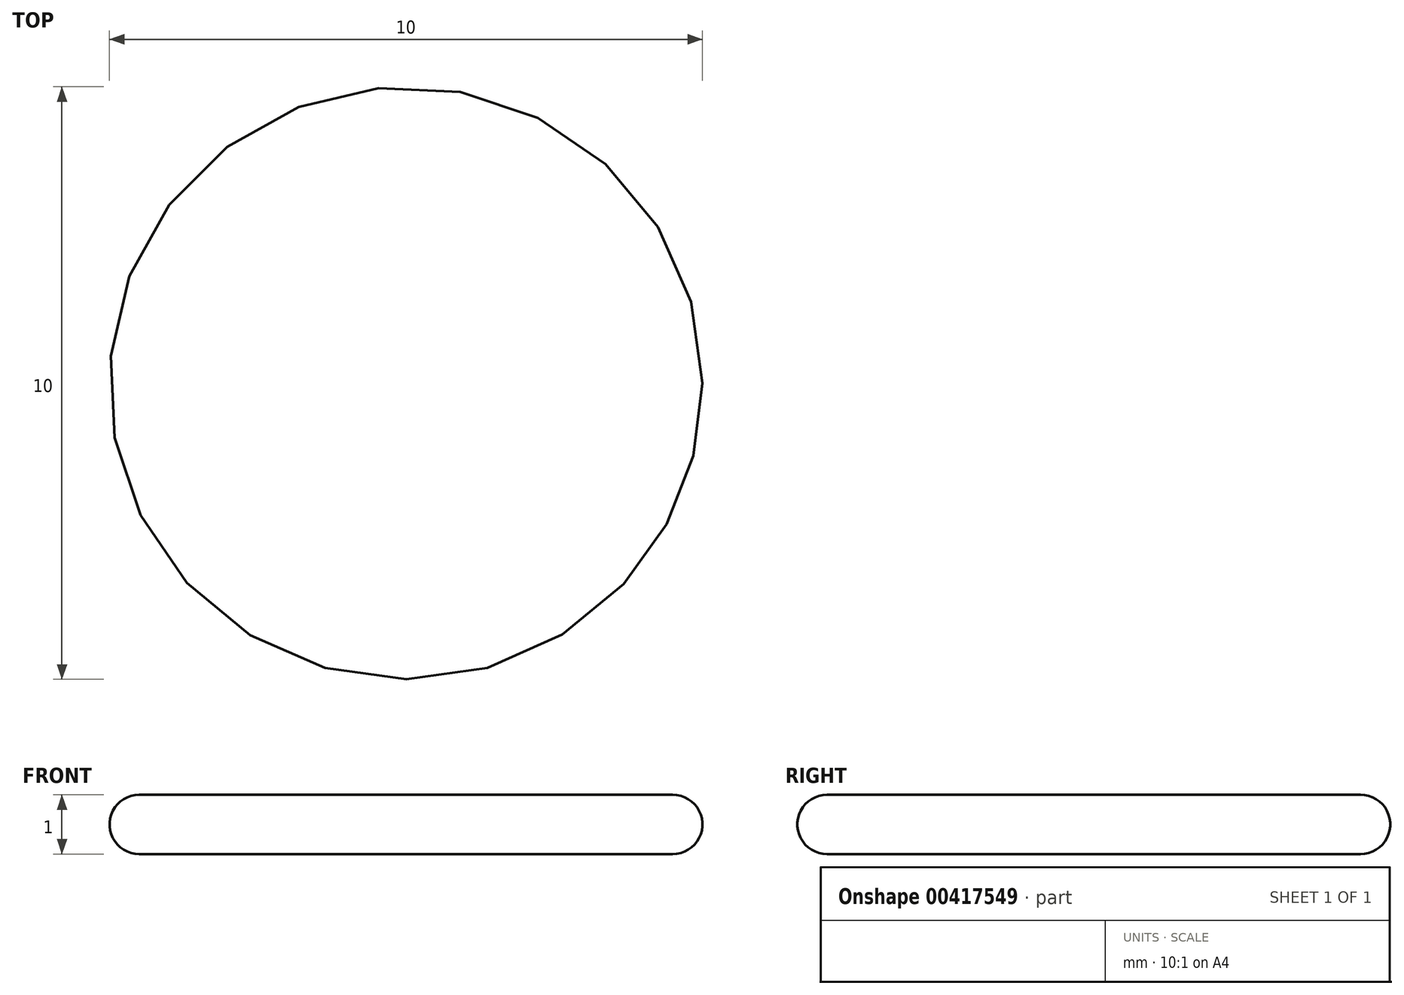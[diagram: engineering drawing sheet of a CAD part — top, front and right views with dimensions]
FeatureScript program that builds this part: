
annotation { "Feature Type Name" : "Feature", "Feature Type Description" : "" }
export const myFeature = defineFeature(function(context is Context, id is Id, definition is map)
    precondition{}
    {
        {
            var Q0;
            Q0=qCreatedBy(makeId("Top.planeOp"),FACE);
            var sketch = newSketch(context, id + "F0", { "sketchPlane" : qUnion([Q0])});
            skCircle(sketch, "E0", {"center": v(0, 0) * mm, "radius": 5 * mm});
            skSolve(sketch);
        }
        {
            var Q0;
            Q0=makeQuery(id+"F0.imprint","IMPRINT",FACE,{"disambiguationData":[TD([[makeQuery(id+"F0.imprint","IMPRINT",EDGE,{"derivedFrom":sQuery(id+"F0.wireOp",EDGE,"E0")}),1.0]])]});
            extrude(context, id + "F1", {"entities" : qUnion([Q0]), "depth" : 1 * mm, "offsetDistance" : 25.4 * mm});
        }
        {
            var Q0;
            Q0=makeQuery(id+"F1.opExtrude","CAP_EDGE",EDGE,{"disambiguationData":[OSD([sQuery(id+"F0.wireOp",EDGE,"E0")])],"isStart":false});
            var Q1;
            Q1=makeQuery(id+"F1.opExtrude","CAP_EDGE",EDGE,{"disambiguationData":[OSD([sQuery(id+"F0.wireOp",EDGE,"E0")])],"isStart":true});
            fillet(context, id + "F2", {"entities" : qUnion([Q0, Q1]), "radius" : .5 * mm, "tangentPropagation" : true, "allowEdgeOverflow" : false});
        }
    });
